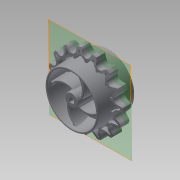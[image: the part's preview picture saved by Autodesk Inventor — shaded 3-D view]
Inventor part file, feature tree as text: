
AUTODESK INVENTOR PART (.ipt)
format: ipt  version: 2013 (Build 170138000, 138)  size: 3,295,744 bytes
history: native  units: in
note: dims shown in document units (in); Inventor stores cm internally (conversion verified against a paired STEP export)
features: other x3, plane x1, imported_body x1, sketch x1, extrude x1
ambient origin geometry x8: Origin, YZ Plane, XZ Plane, XY Plane, X Axis, Y Axis, Z Axis, Center Point
feature tree (7):
  parser-record x1  (decoder bookkeeping rows leaked as tree rows — omitted from the tree; the rows remain in map.json)
  other  "DRIVE-WHEEL1"
  plane  "Work Plane1"
  imported_body  "Base1"
  sketch  "Sketch1"  dims[d0=0.1in d1=1.0in d2=0.0in d3=0.0in d4=0.0in]
  other  "Srf1"
  extrude  "ExtrusionSrf1"  Depth=1.0in TaperAngle=0.0deg
